# Revit family: NAU_Naughtone_Stng_Ruby_Stools1
name_source: partatom
category: Furniture
revit_build: Autodesk Revit 2018 (Build: 20170223_1515(x64)
units: mm (PartAtom-declared; Revit-internal decimal feet)

## family parameters
Always vertical = Yes
Cut with Voids When Loaded = No
OmniClass Number = 23.40.20.00
OmniClass Title = General Furniture and Specialties
Room Calculation Point = No
Shared = Yes
Work Plane-Based = No

## types (4) — shared parameters
AdditionalMaterials = Additional material and finish options available. Please contact Naughtone direct for further information.
Assembly Code = E2020200
AssetType = Movable
BIMObjectName = NAU_Naughtone_Seating_Ruby_Stools
Category = Pr_40_50_12_85 : Stools
Color = Various
DurationUnit = year
Finish = Plastic Shell in 8 RAL colours
IfcExportAs = IfcFurnishingElementType
IfcExportType = STOOL
Keynote = Pr_40_50_12_85
MainColor = Various
ManufacturerAddress = Knaresborough Tech Park, Manse Lane, Knaresborough, HG5 8LF
ManufacturerName = Naughtone
ManufacturerURL = www.naughtone.com
Material = Steel/plastic
NBSDescription = Seating
NBSReference = 45-35-72/352
Name = Seating_Ruby_Stools_Naughtone
NominalLength = 610 mm
ProductInformation = www.naughtone.com/products/ruby/
ReplacementCost = 0.00
Revision = 0
Shape = Rectangular
SustainabilityPerformance = FSC certified. FISP certified. ISO 14001
URL = www.naughtone.com
Uniclass2015Code = Pr_40_50_12_85
Uniclass2015Title = Stools
Version = 1
WarrantyDescription = Request warranty information from naughtone
WarrantyDurationLabor = 7
WarrantyDurationParts = 7
WarrantyDurationUnit = year
zero-valued in all types: Cost

## per-type parameters (varying)
| type | Description | Is4Leg | IsRUBYBSB4L | IsRUBYBSBSL | IsRUBYCHB4L | IsRUBYCHSBSL | Model | ModelNumber | ModelReference | NominalHeight | NominalWidth | Size |
| Ruby Barstool_RUBYBSB4L | Ruby Barstool | Yes | Yes | No | No | No | RUBYBSB4L | RUBYBSB4L | Ruby Barstool | 1095 mm | 535 mm | 610 x 535 x 1095mm |
| Ruby Counter Height Stool_RUBYCHSB4L | Ruby Counter Height Stool | Yes | No | No | Yes | No | RUBYCHSB4L | RUBYCHSB4L | Ruby Counter Height Stool | 995 mm  [stored 3.26444 ft] | 530 mm | 610 x 530 x 995mm |
| Ruby Counter Height Stool on Sled Base_RUBYCHSBSL | Ruby Counter Height Stool on Sled Base | No | No | No | No | Yes | RUBYCHSBSL | RUBYCHSBSL | Ruby Counter Height Stool on Sled Base | 995 mm  [stored 3.26444 ft] | 540 mm | 610 x 540 x 995mm |
| Ruby Barstool on Sled Base_RUBYBSBSL | Ruby Barstool on Sled Base | No | No | Yes | No | No | RUBYBSBSL | RUBYBSBSL | Ruby Barstool on Sled Base | 1090 mm | 565 mm | 610 x 565 x 1090mm |

note: [stored X ft] marks values corroborated as IEEE doubles in the binary element streams (Revit-internal decimal feet)

## geometry (parser evidence)
native form markers: Sweep x2
no freeform markers — native parametric forms only
